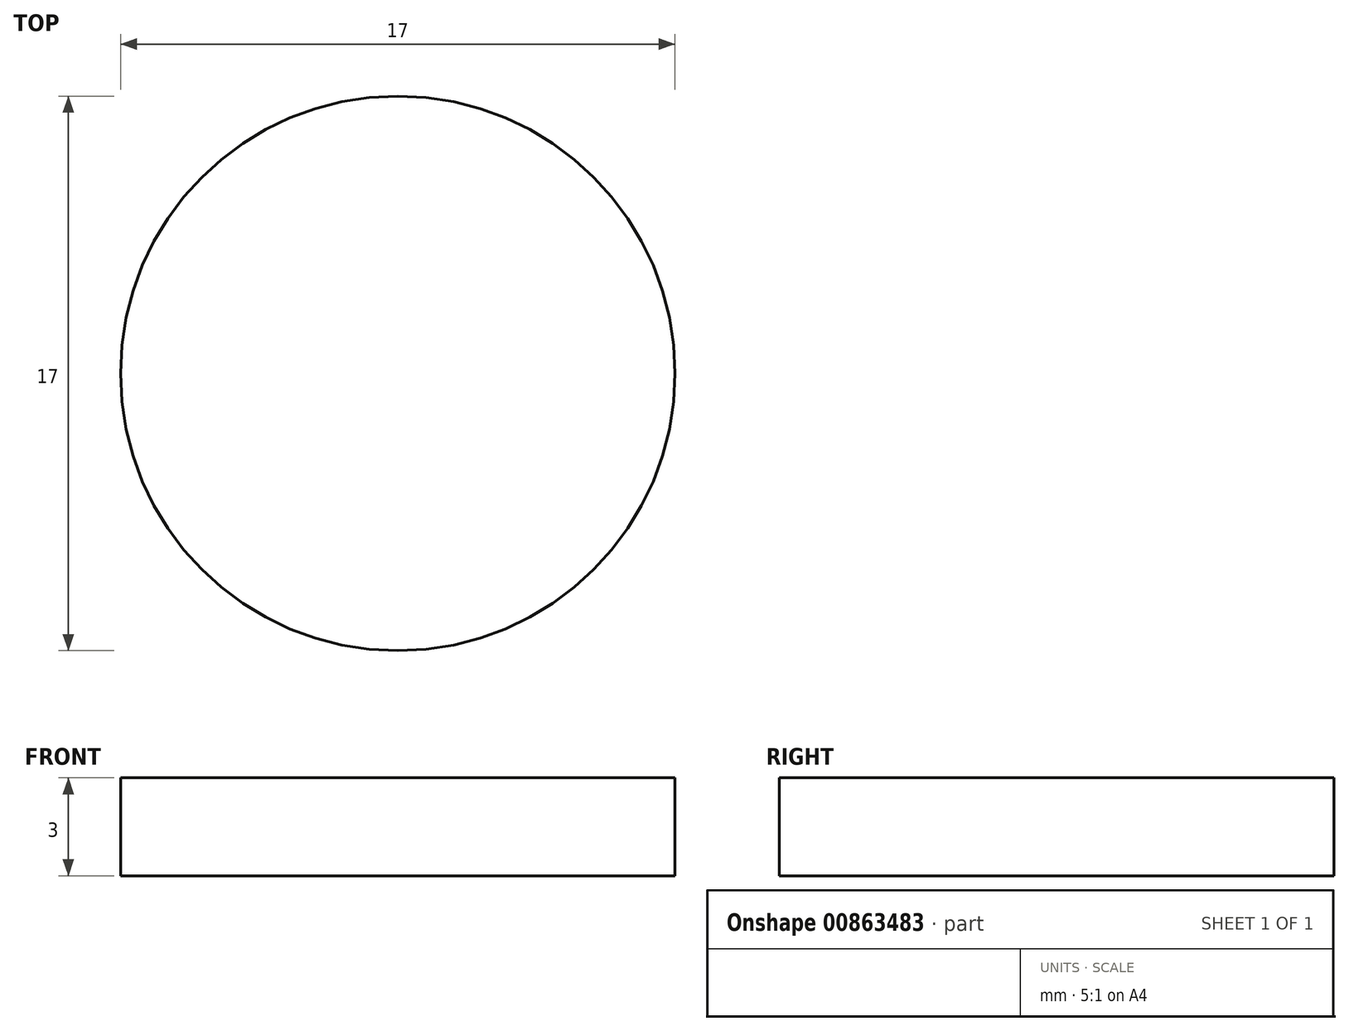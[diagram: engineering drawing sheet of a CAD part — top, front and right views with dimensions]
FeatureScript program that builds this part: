
annotation { "Feature Type Name" : "Feature", "Feature Type Description" : "" }
export const myFeature = defineFeature(function(context is Context, id is Id, definition is map)
    precondition{}
    {
        {
            var Q0;
            Q0=qCreatedBy(makeId("Front.planeOp"),FACE);
            var sketch = newSketch(context, id + "F0", { "sketchPlane" : qUnion([Q0])});
            skLineSegment(sketch, "E0", {"start": v(0, 0) * mm, "end": v(0, 3) * mm});
            skLineSegment(sketch, "E1", {"start": v(0, 0) * mm, "end": v(-8.5, 0) * mm});
            skLineSegment(sketch, "E2", {"start": v(-8.5, 0) * mm, "end": v(-8.5, 3) * mm});
            skLineSegment(sketch, "E3", {"start": v(-8.5, 3) * mm, "end": v(0, 3) * mm});
            skSolve(sketch);
        }
        {
            var Q0;
            Q0 = qSketchRegion(id + "F0", true);
            var Q1;
            Q1=sQuery(id+"F0.wireOp",EDGE,"E0");
            revolve(context, id + "F1", {"surfaceOperationType" : NewSurfaceOperationType.NEW, "entities" : qUnion([Q0]), "axis" : qUnion([Q1]), "revolveType" : RevolveType.FULL});
        }
    });
